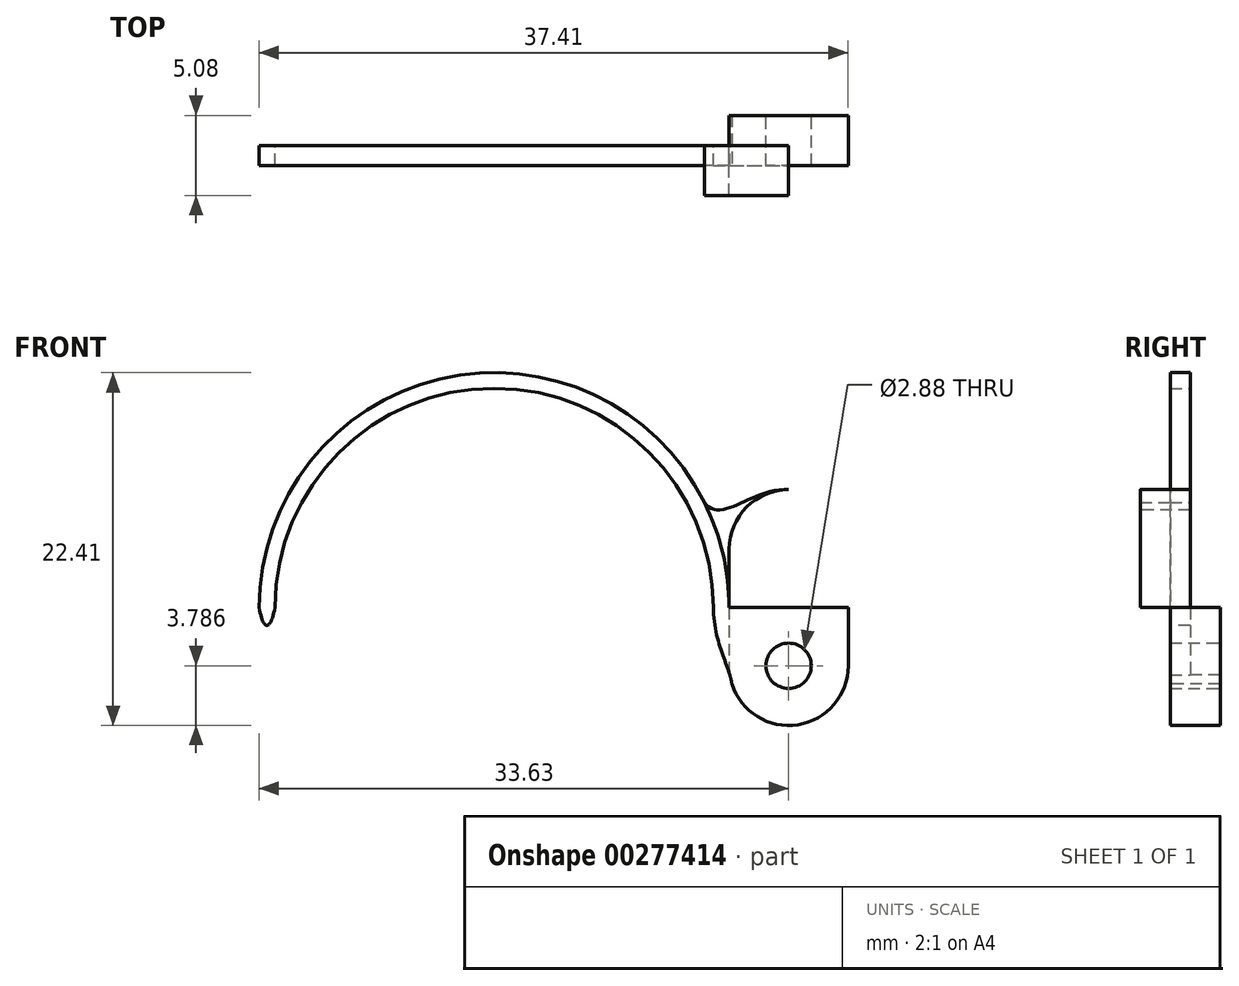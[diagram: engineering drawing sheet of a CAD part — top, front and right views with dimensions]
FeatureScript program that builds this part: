
annotation { "Feature Type Name" : "Feature", "Feature Type Description" : "" }
export const myFeature = defineFeature(function(context is Context, id is Id, definition is map)
    precondition{}
    {
        {
            var Q0;
            Q0=qCreatedBy(makeId("Front.planeOp"),FACE);
            var sketch = newSketch(context, id + "F0", { "sketchPlane" : qUnion([Q0])});
            skLineSegment(sketch, "E0", {"start": v(-3.78, 3.7) * mm, "end": v(-3.78, -3.7) * mm});
            skArc(sketch, "E1", {"start": v(-3.78, 3.7) * mm, "mid": v(0, 7.49) * mm, "end": v(3.78, 3.7) * mm});
            skLineSegment(sketch, "E2", {"start": v(3.78, 3.7) * mm, "end": v(3.78, -3.7) * mm});
            skArc(sketch, "E3", {"start": v(-3.78, -3.7) * mm, "mid": v(0, -7.49) * mm, "end": v(3.78, -3.7) * mm});
            skCircle(sketch, "E4", {"center": v(0, 3.7) * mm, "radius": 1.44 * mm});
            skCircle(sketch, "E5", {"center": v(0, -3.7) * mm, "radius": 1.44 * mm});
            skLineSegment(sketch, "E6", {"start": v(-3.78, 0) * mm, "end": v(3.78, 0) * mm});
            skArc(sketch, "E7", {"start": v(-3.78, 0) * mm, "mid": v(-18.7, 14.92) * mm, "end": v(-33.63, 0) * mm});
            skArc(sketch, "E8", {"start": v(-4.78, 0) * mm, "mid": v(-18.7, 13.92) * mm, "end": v(-32.63, 0) * mm});
            skFitSpline(sketch, "E9", {"points": [v(-4.78, 0) * mm, v(-3.6, -4.86) * mm], "startDerivative": vector(0, -6.31) * mm, "endDerivative": vector(0.55, -3.48) * mm});
            skFitSpline(sketch, "E10", {"points": [v(-5.36, 6.67) * mm, v(0, 7.49) * mm], "startDerivative": vector(3.26, -4.42) * mm, "endDerivative": vector(7.08, -0.39) * mm});
            skFitSpline(sketch, "E11", {"points": [v(-32.63, 0) * mm, v(-33.63, 0) * mm], "startDerivative": vector(-0.76, -4.53) * mm, "endDerivative": vector(-0.7, 4.53) * mm});
            skSolve(sketch);
        }
        {
            var Q0;
            {var subQ1=sQuery(id+"F0.wireOp",EDGE,"E1");Q0=makeQuery(id+"F0.imprint","IMPRINT",FACE,{"disambiguationData":[TD([[makeQuery(id+"F0.imprint","IMPRINT",EDGE,{"derivedFrom":subQ1}),-1.0]])]});}
            extrude(context, id + "F1", {"entities" : qUnion([Q0]), "depth" : 2.54 * mm, "hasSecondDirection" : true, "secondDirectionOppositeDirection" : true, "secondDirectionDepth" : 0.64 * mm});
        }
        {
            var Q0;
            {var subQ0=sQuery(id+"F0.wireOp",EDGE,"E3");Q0=makeQuery(id+"F0.imprint","IMPRINT",FACE,{"disambiguationData":[TD([[makeQuery(id+"F0.imprint","IMPRINT",EDGE,{"derivedFrom":subQ0}),1.0]])]});}
            extrude(context, id + "F2", {"entities" : qUnion([Q0]), "operationType" : NewBodyOperationType.ADD, "depth" : 0.64 * mm, "hasSecondDirection" : true, "secondDirectionOppositeDirection" : true, "secondDirectionDepth" : 2.54 * mm});
        }
        {
            var Q0;
            {var subQ5=sQuery(id+"F0.wireOp",EDGE,"E10");Q0=makeQuery(id+"F0.imprint","IMPRINT",FACE,{"disambiguationData":[TD([[makeQuery(id+"F0.imprint","IMPRINT",EDGE,{"derivedFrom":subQ5}),-1.0]])]});}
            var Q1;
            {var subQ9=sQuery(id+"F0.wireOp",EDGE,"E8");Q1=makeQuery(id+"F0.imprint","IMPRINT",FACE,{"disambiguationData":[TD([[makeQuery(id+"F0.imprint","IMPRINT",EDGE,{"derivedFrom":subQ9}),-1.0]])]});}
            extrude(context, id + "F3", {"entities" : qUnion([Q0, Q1]), "operationType" : NewBodyOperationType.ADD, "depth" : 0.64 * mm, "hasSecondDirection" : true, "secondDirectionOppositeDirection" : true, "secondDirectionDepth" : 0.64 * mm});
        }
    });
